# Revit family: GR_Решетка_РАГ-РН_Приток_R21
name_source: partatom
category: Воздухораспределители
units: mm (PartAtom-declared; Revit-internal decimal feet)

## family parameters
Всегда вертикально = Да
Заголовок OmniClass = Diffusers, Registers, and Grilles
На основе рабочей плоскости = Нет
Номер OmniClass = 23.75.70.21.27.11
Общий = Нет
При загрузке вырезать с полостями = Да
Размер круглого соединителя = Использовать диаметр
Тип детали = Нормальный
Точка принадлежности помещению = Нет

## types (1)
- РАГ-РН
    ADSK_URL страницы изделия = https://grilles.ru
    ADSK_Автор = THE GRILLES
    ADSK_Версия Revit = 2021
    ADSK_Версия семейства = v1
    ADSK_Единица измерения = шт.
    ADSK_Завод-изготовитель = ООО "ВЕНТРЕШЕТКИКОМ"
    ADSK_Код изделия = 002030
    ADSK_Количество = 1
    ADSK_Наименование = Накладная регулируемая решетка приточная РАГ-РН
    GR_Материал решетки = Сталь, RAL 9016M, белый
    URL = https://grilles.ru
    Изготовитель = ООО "ВЕНТРЕШЕТКИКОМ"
    КЖС = 0.79
    Описание = Однорядная регулируемая накладная решетка РАГ-РН
по назначению и функциональности полностью повторяет решетку
РАГ. Единственным конструктивным отличием является накладной тип
исполнения, ее рамка сделана без внешнего фланца. Решетка РАГ-РН
накладывается на проем, либо полностью утапливается в проеме.
    Отметка по умолчанию = 0 мм
